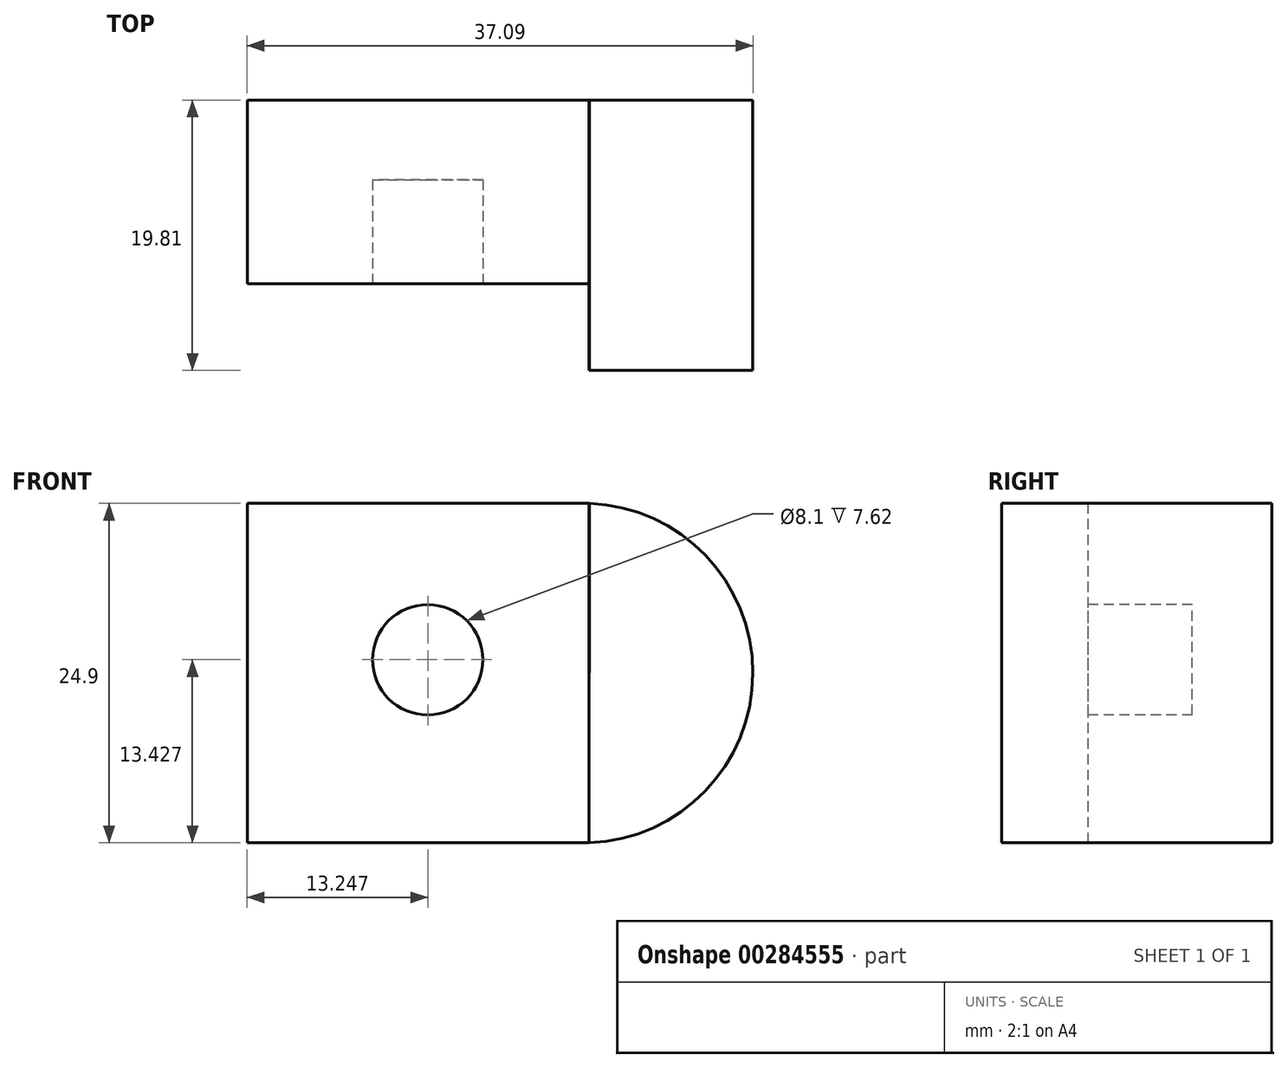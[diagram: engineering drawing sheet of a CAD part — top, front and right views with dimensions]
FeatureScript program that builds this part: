
annotation { "Feature Type Name" : "Feature", "Feature Type Description" : "" }
export const myFeature = defineFeature(function(context is Context, id is Id, definition is map)
    precondition{}
    {
        {
            var Q0;
            Q0=qCreatedBy(makeId("Front.planeOp"),FACE);
            var sketch = newSketch(context, id + "F0", { "sketchPlane" : qUnion([Q0])});
            skLineSegment(sketch, "E0", {"start": v(-34.45, 0) * mm, "end": v(-34.45, 24.9) * mm});
            skLineSegment(sketch, "E1", {"start": v(-34.45, 24.9) * mm, "end": v(-9.4, 24.9) * mm});
            skLineSegment(sketch, "E2", {"start": v(-9.4, 24.9) * mm, "end": v(-9.4, 0) * mm});
            skLineSegment(sketch, "E3", {"start": v(-9.4, 0) * mm, "end": v(-34.45, 0) * mm});
            skArc(sketch, "E4", {"start": v(-9.4, 0) * mm, "mid": v(3.05, 12.45) * mm, "end": v(-9.4, 24.9) * mm});
            skSolve(sketch);
        }
        {
            var Q0;
            Q0=makeQuery(id+"F0.imprint","IMPRINT",FACE,{"disambiguationData":[TD([[makeQuery(id+"F0.imprint","IMPRINT",EDGE,{"derivedFrom":sQuery(id+"F0.wireOp",EDGE,"E0")}),-1.0]])]});
            extrude(context, id + "F1", {"entities" : qUnion([Q0]), "depth" : 12.7 * mm, "hasSecondDirection" : true, "secondDirectionOppositeDirection" : true, "secondDirectionDepth" : 0.76 * mm});
        }
        {
            var Q0;
            Q0=qCreatedBy(makeId("Front.planeOp"),FACE);
            var sketch = newSketch(context, id + "F2", { "sketchPlane" : qUnion([Q0])});
            skLineSegment(sketch, "E5", {"start": v(-9.36, 24.9) * mm, "end": v(-9.4, 0) * mm});
            skArc(sketch, "E6", {"start": v(-9.4, 0) * mm, "mid": v(2.64, 12.43) * mm, "end": v(-9.36, 24.9) * mm});
            skSolve(sketch);
        }
        {
            var Q0;
            Q0=makeQuery(id+"F2.imprint","IMPRINT",FACE,{"disambiguationData":[TD([[makeQuery(id+"F2.imprint","IMPRINT",EDGE,{"derivedFrom":sQuery(id+"F2.wireOp",EDGE,"E5")}),1.0]])]});
            extrude(context, id + "F3", {"entities" : qUnion([Q0]), "depth" : 19.05 * mm, "hasSecondDirection" : true, "secondDirectionOppositeDirection" : true, "secondDirectionDepth" : 0.76 * mm});
        }
        {
            var Q0;
            Q0=makeQuery(id+"F1.opExtrude","CAP_FACE",FACE,{"disambiguationData":[OSD([sQuery(id+"F0.wireOp",EDGE,"E0"),sQuery(id+"F0.wireOp",EDGE,"E1"),sQuery(id+"F0.wireOp",EDGE,"E2"),sQuery(id+"F0.wireOp",EDGE,"E3")])],"isStart":false});
            var sketch = newSketch(context, id + "F4", { "sketchPlane" : qUnion([Q0])});
            skCircle(sketch, "E7", {"center": v(-21.2, 13.43) * mm, "radius": 4.05 * mm});
            skSolve(sketch);
        }
        {
            var Q0;
            Q0=makeQuery(id+"F4.imprint","IMPRINT",FACE,{"disambiguationData":[TD([[makeQuery(id+"F4.imprint","IMPRINT",EDGE,{"derivedFrom":sQuery(id+"F4.wireOp",EDGE,"E7")}),1.0]])]});
            extrude(context, id + "F5", {"entities" : qUnion([Q0]), "operationType" : NewBodyOperationType.REMOVE, "oppositeDirection" : true, "depth" : 7.62 * mm});
        }
    });
